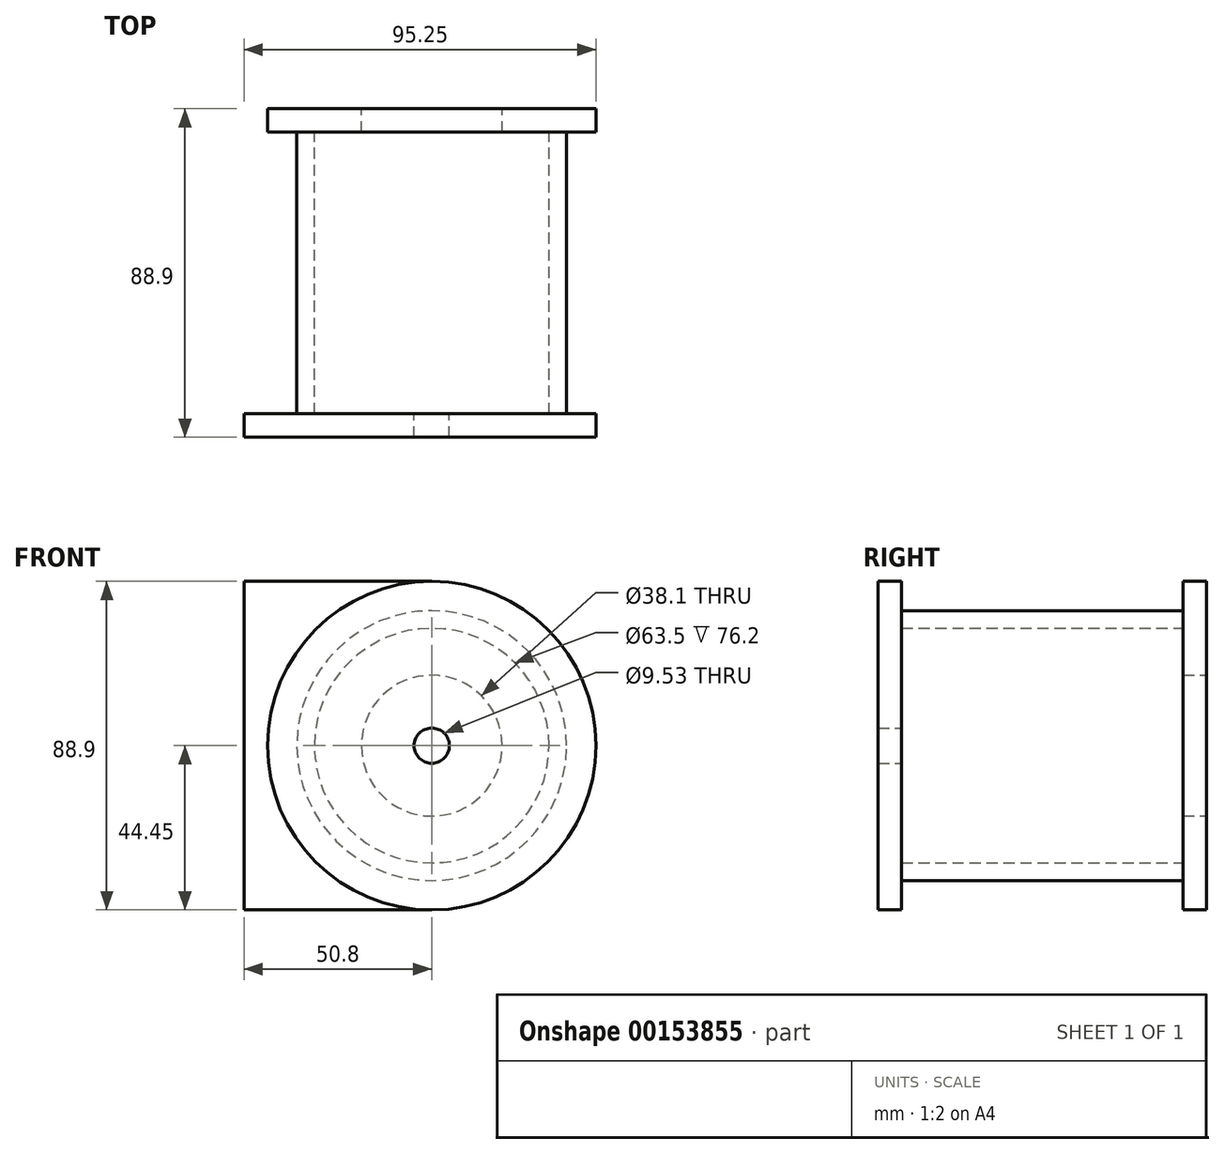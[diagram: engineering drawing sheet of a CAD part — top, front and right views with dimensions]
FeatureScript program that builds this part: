
annotation { "Feature Type Name" : "Feature", "Feature Type Description" : "" }
export const myFeature = defineFeature(function(context is Context, id is Id, definition is map)
    precondition{}
    {
        {
            var Q0;
            Q0=qCreatedBy(makeId("Front.planeOp"),FACE);
            var sketch = newSketch(context, id + "F0", { "sketchPlane" : qUnion([Q0])});
            skCircle(sketch, "E0", {"center": v(0, 0) * mm, "radius": 44.45 * mm});
            skCircle(sketch, "E1", {"center": v(0, 0) * mm, "radius": 19.05 * mm});
            skSolve(sketch);
        }
        {
            var Q0;
            Q0=makeQuery(id+"F0.imprint","IMPRINT",FACE,{"disambiguationData":[TD([[makeQuery(id+"F0.imprint","IMPRINT",EDGE,{"derivedFrom":sQuery(id+"F0.wireOp",EDGE,"E0")}),1.0]])]});
            extrude(context, id + "F1", {"entities" : qUnion([Q0]), "depth" : 6.35 * mm});
        }
        {
            var Q0;
            Q0=makeQuery(id+"F1.opExtrude","CAP_FACE",FACE,{"disambiguationData":[OSD([sQuery(id+"F0.wireOp",EDGE,"E0"),sQuery(id+"F0.wireOp",EDGE,"E1")])],"isStart":false});
            var sketch = newSketch(context, id + "F2", { "sketchPlane" : qUnion([Q0])});
            skCircle(sketch, "E2", {"center": v(0, 0) * mm, "radius": 31.75 * mm});
            skCircle(sketch, "E3", {"center": v(0, 0) * mm, "radius": 36.51 * mm});
            skSolve(sketch);
        }
        {
            var Q0;
            Q0=makeQuery(id+"F2.imprint","IMPRINT",FACE,{"disambiguationData":[TD([[makeQuery(id+"F2.imprint","IMPRINT",EDGE,{"derivedFrom":sQuery(id+"F2.wireOp",EDGE,"E2")}),-1.0]])]});
            extrude(context, id + "F3", {"entities" : qUnion([Q0]), "operationType" : NewBodyOperationType.ADD, "depth" : 76.2 * mm});
        }
        {
            var Q0;
            Q0=makeQuery(id+"F3.opExtrude","CAP_FACE",FACE,{"disambiguationData":[OSD([sQuery(id+"F2.wireOp",EDGE,"E2"),sQuery(id+"F2.wireOp",EDGE,"E3")])],"isStart":false});
            var sketch = newSketch(context, id + "F4", { "sketchPlane" : qUnion([Q0])});
            skCircle(sketch, "E4", {"center": v(0, 0) * mm, "radius": 44.45 * mm});
            skCircle(sketch, "E5", {"center": v(0, 0) * mm, "radius": 4.76 * mm});
            skLineSegment(sketch, "E6.bottom", {"start": v(0, 44.45) * mm, "end": v(-50.8, 44.45) * mm});
            skLineSegment(sketch, "E6.top", {"start": v(0, -44.45) * mm, "end": v(-50.8, -44.45) * mm});
            skLineSegment(sketch, "E6.left", {"start": v(0, 44.45) * mm, "end": v(0, -44.45) * mm});
            skLineSegment(sketch, "E6.right", {"start": v(-50.8, 44.45) * mm, "end": v(-50.8, -44.45) * mm});
            skSolve(sketch);
        }
        {
            var Q0;
            Q0 = qSketchRegion(id + "F4", true);
            extrude(context, id + "F5", {"entities" : qUnion([Q0]), "operationType" : NewBodyOperationType.ADD, "depth" : 6.35 * mm});
        }
        {
            var Q0;
            Q0=makeQuery(id+"F5.opExtrude","CAP_FACE",FACE,{"disambiguationData":[OSD([sQuery(id+"F4.wireOp",EDGE,"E4"),sQuery(id+"F4.wireOp",EDGE,"E5")])],"isStart":false});
            var sketch = newSketch(context, id + "F6", { "sketchPlane" : qUnion([Q0])});
            skLineSegment(sketch, "E7.bottom", {"start": v(38.1, 25.4) * mm, "end": v(44.45, 25.4) * mm});
            skLineSegment(sketch, "E7.top", {"start": v(38.1, -25.4) * mm, "end": v(44.45, -25.4) * mm});
            skLineSegment(sketch, "E7.left", {"start": v(38.1, 25.4) * mm, "end": v(38.1, -25.4) * mm});
            skLineSegment(sketch, "E7.right", {"start": v(44.45, 25.4) * mm, "end": v(44.45, -25.4) * mm});
            skSolve(sketch);
        }
        {
            var Q0;
            Q0 = qSketchRegion(id + "F6", true);
            extrude(context, id + "F7", {"entities" : qUnion([Q0]), "depth" : 76.2 * mm});
        }
        {
            var Q0;
            Q0=makeQuery(id+"F7.opExtrude","SWEPT_BODY",BODY,{"disambiguationData":[OSD([sQuery(id+"F6.wireOp",EDGE,"E7.bottom"),sQuery(id+"F6.wireOp",EDGE,"E7.top"),sQuery(id+"F6.wireOp",EDGE,"E7.left"),sQuery(id+"F6.wireOp",EDGE,"E7.right")])]});
            deleteBodies(context, id + "F8", {"entities" : qUnion([Q0])});
        }
    });
